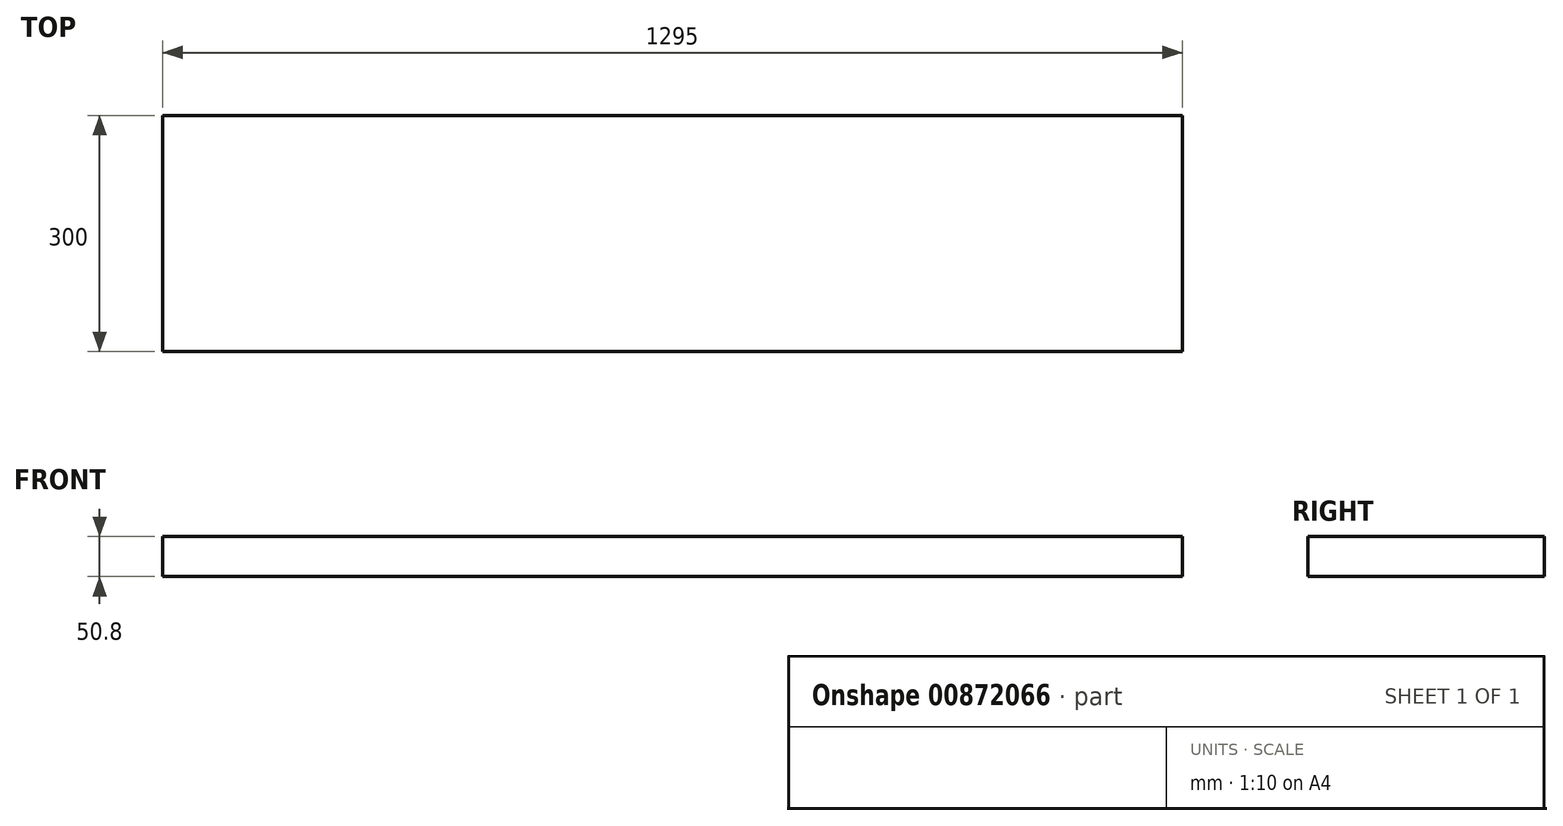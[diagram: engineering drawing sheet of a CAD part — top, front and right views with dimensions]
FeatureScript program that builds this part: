
annotation { "Feature Type Name" : "Feature", "Feature Type Description" : "" }
export const myFeature = defineFeature(function(context is Context, id is Id, definition is map)
    precondition{}
    {
        {
            var Q0;
            Q0=qCreatedBy(makeId("Top.planeOp"),FACE);
            var sketch = newSketch(context, id + "F0", { "sketchPlane" : qUnion([Q0])});
            skLineSegment(sketch, "E0.bottom", {"start": v(0, 0) * mm, "end": v(1295, 0) * mm});
            skLineSegment(sketch, "E0.top", {"start": v(0, 300) * mm, "end": v(1295, 300) * mm});
            skLineSegment(sketch, "E0.left", {"start": v(0, 0) * mm, "end": v(0, 300) * mm});
            skLineSegment(sketch, "E0.right", {"start": v(1295, 0) * mm, "end": v(1295, 300) * mm});
            skSolve(sketch);
        }
        {
            var Q0;
            Q0=qSketchRegion(id+"F0",true);
            extrude(context, id + "F1", {"entities" : qUnion([Q0]), "depth" : 50.8 * mm, "offsetDistance" : 25 * mm});
        }
    });
